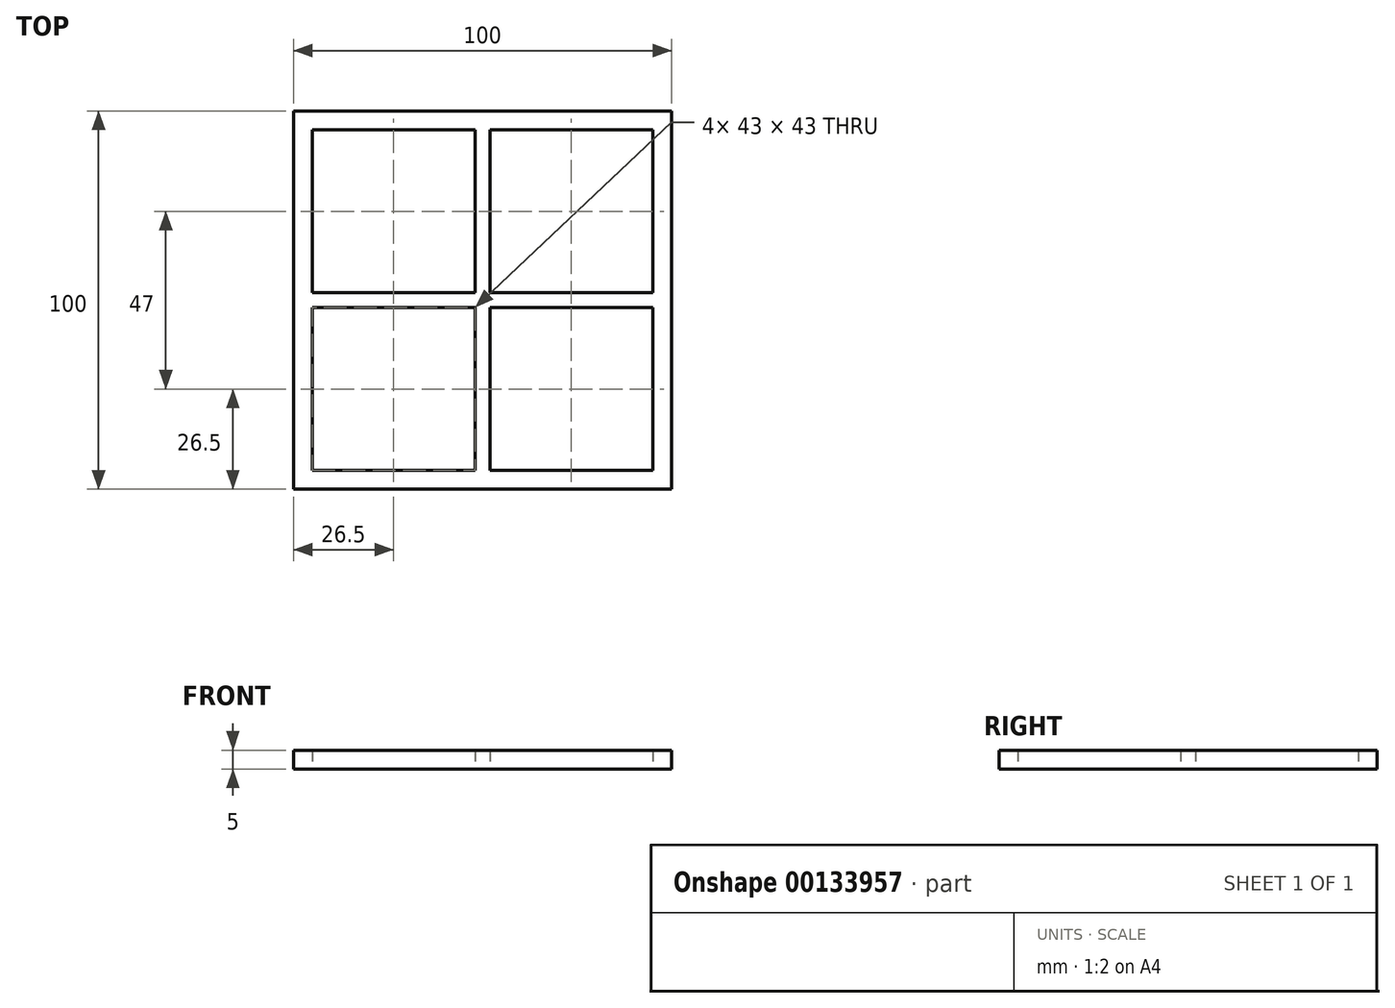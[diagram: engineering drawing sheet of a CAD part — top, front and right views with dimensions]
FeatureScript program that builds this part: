
annotation { "Feature Type Name" : "Feature", "Feature Type Description" : "" }
export const myFeature = defineFeature(function(context is Context, id is Id, definition is map)
    precondition{}
    {
        {
            var Q0;
            Q0=qCreatedBy(makeId("Top.planeOp"),FACE);
            var sketch = newSketch(context, id + "F0", { "sketchPlane" : qUnion([Q0])});
            skLineSegment(sketch, "E0.bottom", {"start": v(45, 45) * mm, "end": v(2, 45) * mm});
            skLineSegment(sketch, "E0.top", {"start": v(45, -45) * mm, "end": v(2, -45) * mm});
            skLineSegment(sketch, "E0.left", {"start": v(45, 45) * mm, "end": v(45, 2) * mm});
            skLineSegment(sketch, "E0.right", {"start": v(-45, 45) * mm, "end": v(-45, 2) * mm});
            skPoint(sketch, "E0.middle", {"position": v(0, 0) * mm});
            skLineSegment(sketch, "E1.0", {"start": v(-50, 50) * mm, "end": v(-50, -50) * mm});
            skLineSegment(sketch, "E1.1", {"start": v(50, 50) * mm, "end": v(-50, 50) * mm});
            skLineSegment(sketch, "E1.2", {"start": v(50, 50) * mm, "end": v(50, -50) * mm});
            skLineSegment(sketch, "E1.3", {"start": v(50, -50) * mm, "end": v(-50, -50) * mm});
            skLineSegment(sketch, "E2.bottom", {"start": v(45, -2) * mm, "end": v(2, -2) * mm});
            skLineSegment(sketch, "E2.top", {"start": v(45, 2) * mm, "end": v(2, 2) * mm});
            skLineSegment(sketch, "E3.left", {"start": v(2, -45) * mm, "end": v(2, -2) * mm});
            skLineSegment(sketch, "E3.right", {"start": v(-2, -45) * mm, "end": v(-2, -2) * mm});
            skLineSegment(sketch, "E4.trimOffspring", {"start": v(-2, 45) * mm, "end": v(-45, 45) * mm});
            skLineSegment(sketch, "E5.trimOffspring", {"start": v(45, -2) * mm, "end": v(45, -45) * mm});
            skLineSegment(sketch, "E6.trimOffspring", {"start": v(-45, -2) * mm, "end": v(-45, -45) * mm});
            skLineSegment(sketch, "E7.trimOffspring", {"start": v(-2, -45) * mm, "end": v(-45, -45) * mm});
            skLineSegment(sketch, "E8.trimOffspring", {"start": v(-2, 2) * mm, "end": v(-2, 45) * mm});
            skLineSegment(sketch, "E9.trimOffspring", {"start": v(-2, 2) * mm, "end": v(-45, 2) * mm});
            skLineSegment(sketch, "E10.trimOffspring", {"start": v(2, 2) * mm, "end": v(2, 45) * mm});
            skLineSegment(sketch, "E11.trimOffspring", {"start": v(-2, -2) * mm, "end": v(-45, -2) * mm});
            skSolve(sketch);
        }
        {
            var Q0;
            Q0 = qSketchRegion(id + "F0", true);
            extrude(context, id + "F1", {"entities" : qUnion([Q0]), "depth" : 5 * mm});
        }
    });
